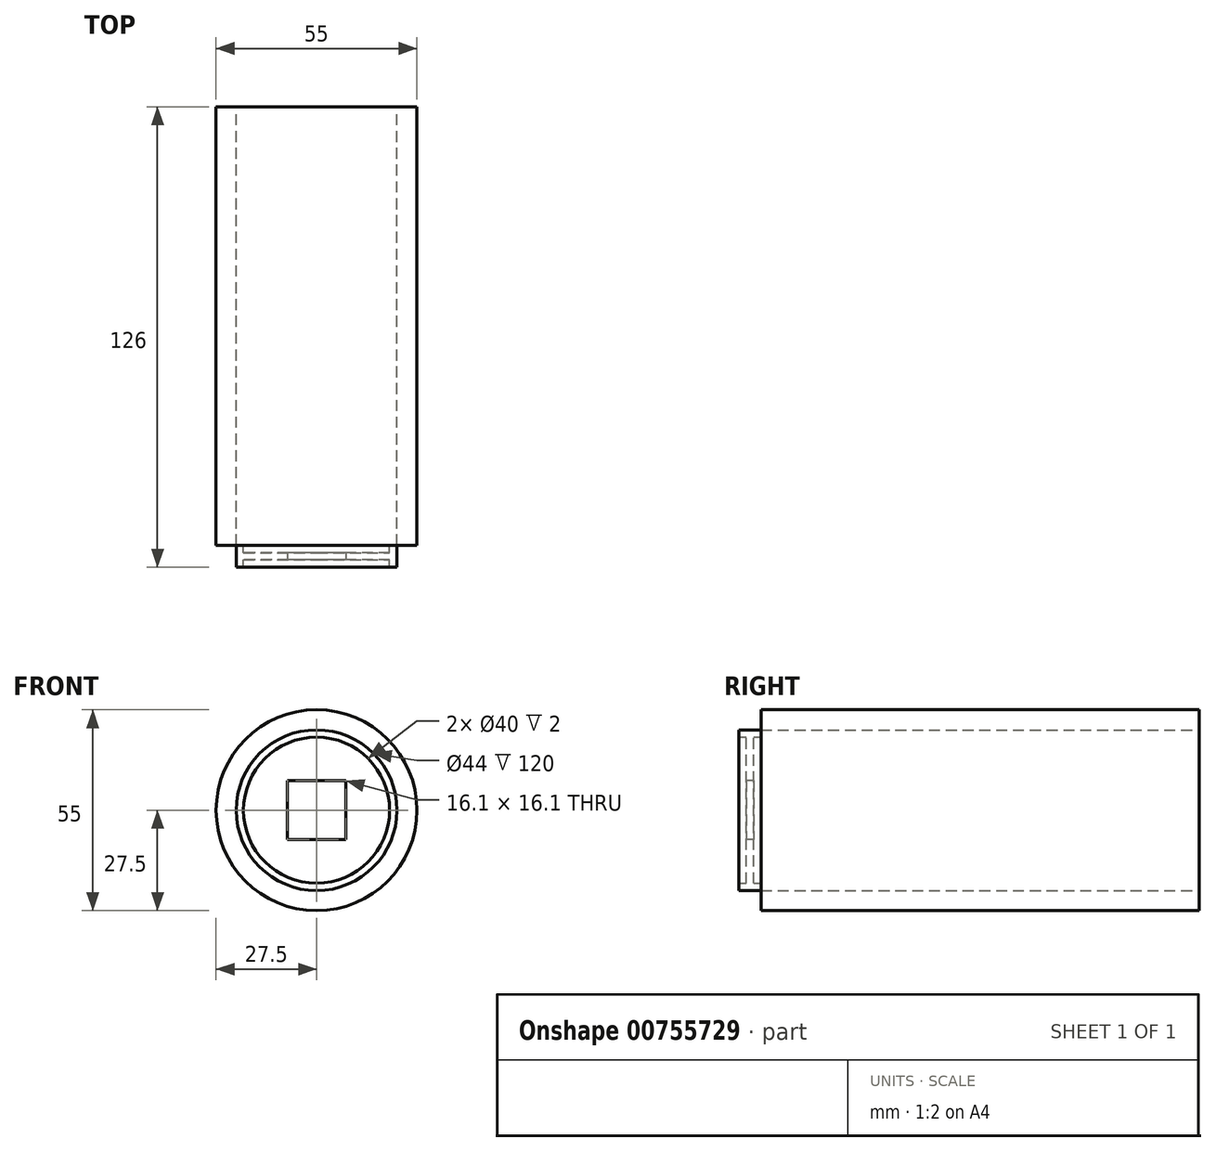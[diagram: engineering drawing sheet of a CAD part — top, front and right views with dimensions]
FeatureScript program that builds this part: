
annotation { "Feature Type Name" : "Feature", "Feature Type Description" : "" }
export const myFeature = defineFeature(function(context is Context, id is Id, definition is map)
    precondition{}
    {
        {
            assignVariable(context, id + "F0", {"name" : "l", "anyValue" : 120});
        }
        {
            var Q0;
            Q0=qCreatedBy(makeId("Front.planeOp"),FACE);
            var sketch = newSketch(context, id + "F1", { "sketchPlane" : qUnion([Q0])});
            skCircle(sketch, "E0", {"center": v(0, 0) * mm, "radius": 27.5 * mm});
            skCircle(sketch, "E1", {"center": v(0, 0) * mm, "radius": 22 * mm});
            skSolve(sketch);
        }
        {
            var Q0;
            Q0=makeQuery(id+"F1.imprint","IMPRINT",FACE,{"disambiguationData":[TD([[makeQuery(id+"F1.imprint","IMPRINT",EDGE,{"derivedFrom":sQuery(id+"F1.wireOp",EDGE,"E0")}),1.0]])]});
            extrude(context, id + "F2", {"entities" : qUnion([Q0]), "depth" : getVariable(context, 'l') * mm, "offsetDistance" : 25 * mm});
        }
        {
            var Q0;
            Q0=makeQuery(id+"F2.opExtrude","CAP_FACE",FACE,{"disambiguationData":[OSD([sQuery(id+"F1.wireOp",EDGE,"E0"),sQuery(id+"F1.wireOp",EDGE,"E1")])],"isStart":false});
            var sketch = newSketch(context, id + "F3", { "sketchPlane" : qUnion([Q0])});
            skCircle(sketch, "E2", {"center": v(0, 0) * mm, "radius": 22 * mm});
            skLineSegment(sketch, "E3.bottom", {"start": v(8.05, 8.05) * mm, "end": v(-8.05, 8.05) * mm});
            skLineSegment(sketch, "E3.top", {"start": v(8.05, -8.05) * mm, "end": v(-8.05, -8.05) * mm});
            skLineSegment(sketch, "E3.left", {"start": v(8.05, 8.05) * mm, "end": v(8.05, -8.05) * mm});
            skLineSegment(sketch, "E3.right", {"start": v(-8.05, 8.05) * mm, "end": v(-8.05, -8.05) * mm});
            skCircle(sketch, "E4", {"center": v(0, 0) * mm, "radius": 20 * mm});
            skSolve(sketch);
        }
        {
            var Q0;
            Q0 = qSketchRegion(id + "F3", true);
            extrude(context, id + "F4", {"entities" : qUnion([Q0]), "depth" : 6 * mm, "offsetDistance" : 25 * mm});
        }
        {
            var Q0;
            Q0=makeQuery(id+"F4.opExtrude","CAP_FACE",FACE,{"disambiguationData":[OSD([sQuery(id+"F3.wireOp",EDGE,"E2"),sQuery(id+"F3.wireOp",EDGE,"E4")])],"isStart":false});
            cPlane(context, id + "F5", {"entities" : qUnion([Q0]), "cplaneType" : CPlaneType.OFFSET, "offset" : 2 * mm, "oppositeDirection" : true, "width" : 150 * mm, "height" : 150 * mm});
        }
        {
            var Q0;
            Q0=makeQuery(id+"F3.imprint","IMPRINT",FACE,{"disambiguationData":[TD([[makeQuery(id+"F3.imprint","IMPRINT",EDGE,{"derivedFrom":sQuery(id+"F3.wireOp",EDGE,"E2")}),1.0]])]});
            extrude(context, id + "F6", {"entities" : qUnion([Q0]), "operationType" : NewBodyOperationType.ADD, "depth" : 2 * mm, "offsetDistance" : 25 * mm});
        }
        {
            var Q0;
            Q0=qCreatedBy(id+"F5.planeOp",FACE);
            var sketch = newSketch(context, id + "F7", { "sketchPlane" : qUnion([Q0])});
            skCircle(sketch, "E5.0", {"center": v(0, 0) * mm, "radius": 20 * mm});
            skLineSegment(sketch, "E6.0", {"start": v(8.05, 8.05) * mm, "end": v(-8.05, 8.05) * mm});
            skLineSegment(sketch, "E7.0", {"start": v(8.05, -8.05) * mm, "end": v(-8.05, -8.05) * mm});
            skPoint(sketch, "E8.0", {"position": v(8.05, -8.05) * mm});
            skPoint(sketch, "E9.0", {"position": v(8.05, 0) * mm});
            skPoint(sketch, "E10.0", {"position": v(-8.05, 0) * mm});
            skLineSegment(sketch, "E11.0", {"start": v(-8.05, 8.05) * mm, "end": v(-8.05, -8.05) * mm});
            skLineSegment(sketch, "E12.0", {"start": v(8.05, 8.05) * mm, "end": v(8.05, -8.05) * mm});
            skSolve(sketch);
        }
        {
            var Q0;
            Q0=makeQuery(id+"F7.imprint","IMPRINT",FACE,{"disambiguationData":[TD([[makeQuery(id+"F7.imprint","IMPRINT",EDGE,{"derivedFrom":sQuery(id+"F7.wireOp",EDGE,"E5.0")}),1.0]])]});
            extrude(context, id + "F8", {"entities" : qUnion([Q0]), "operationType" : NewBodyOperationType.ADD, "oppositeDirection" : true, "depth" : 2 * mm, "offsetDistance" : 25 * mm});
        }
    });
